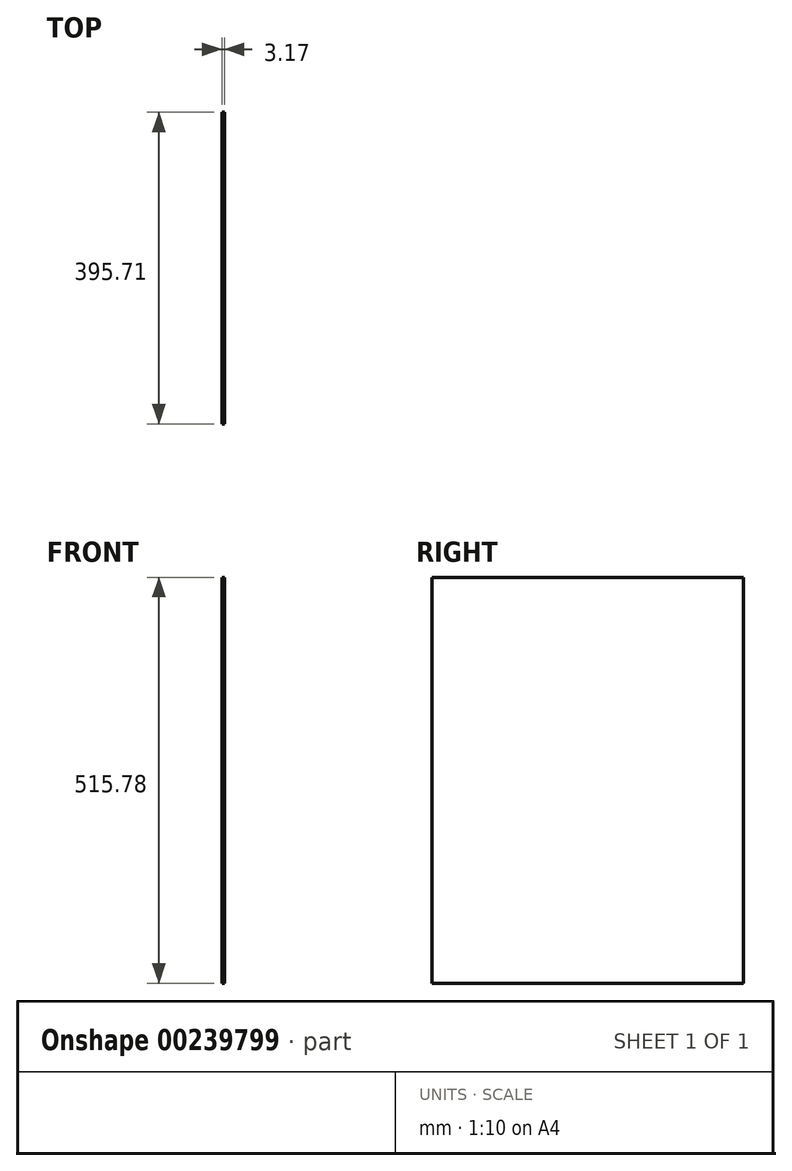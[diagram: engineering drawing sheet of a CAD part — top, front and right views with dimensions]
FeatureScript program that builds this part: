
annotation { "Feature Type Name" : "Feature", "Feature Type Description" : "" }
export const myFeature = defineFeature(function(context is Context, id is Id, definition is map)
    precondition{}
    {
        {
            var Q0;
            Q0=qCreatedBy(makeId("Right.planeOp"),FACE);
            var sketch = newSketch(context, id + "F0", { "sketchPlane" : qUnion([Q0])});
            skLineSegment(sketch, "E0.bottom", {"start": v(-212.48, -246.5) * mm, "end": v(183.23, -246.5) * mm});
            skLineSegment(sketch, "E0.top", {"start": v(-212.48, 269.28) * mm, "end": v(183.23, 269.28) * mm});
            skLineSegment(sketch, "E0.left", {"start": v(-212.48, -246.5) * mm, "end": v(-212.48, 269.28) * mm});
            skLineSegment(sketch, "E0.right", {"start": v(183.23, -246.5) * mm, "end": v(183.23, 269.28) * mm});
            skPoint(sketch, "E0.middle", {"position": v(-14.62, 11.39) * mm});
            skSolve(sketch);
        }
        {
            var Q0;
            Q0 = qSketchRegion(id + "F0", true);
            extrude(context, id + "F1", {"entities" : qUnion([Q0]), "depth" : 3.17 * mm});
        }
    });
